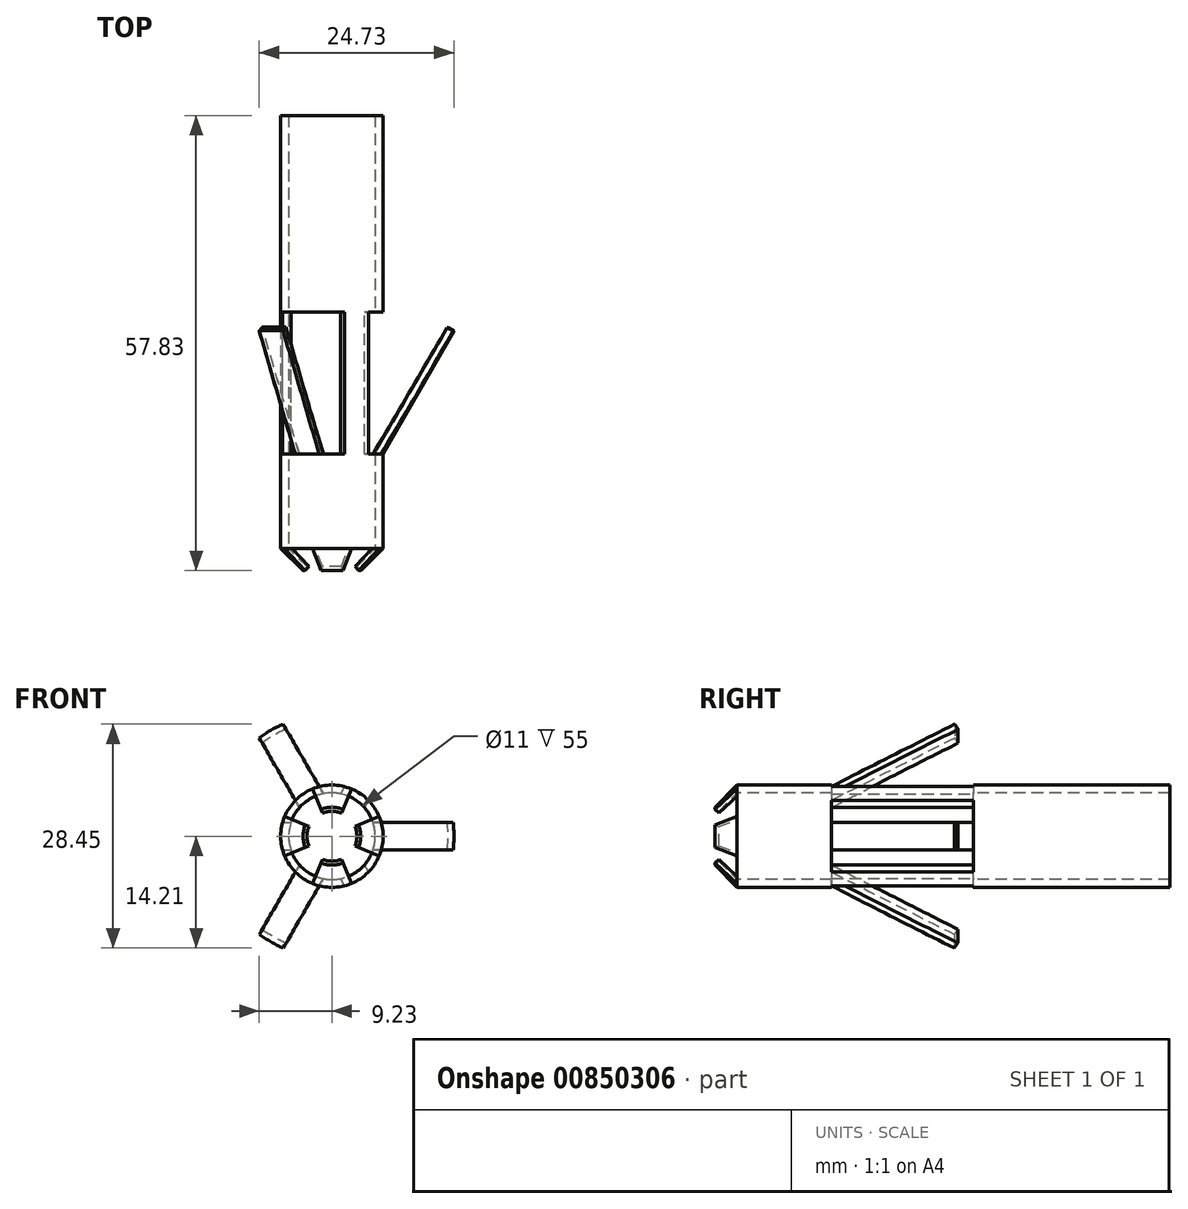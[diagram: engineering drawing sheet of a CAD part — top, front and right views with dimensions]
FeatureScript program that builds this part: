
annotation { "Feature Type Name" : "Feature", "Feature Type Description" : "" }
export const myFeature = defineFeature(function(context is Context, id is Id, definition is map)
    precondition{}
    {
        {
            var Q0;
            Q0=qCreatedBy(makeId("Front.planeOp"),FACE);
            var sketch = newSketch(context, id + "F0", { "sketchPlane" : qUnion([Q0])});
            skCircle(sketch, "E0", {"center": v(0, 0) * mm, "radius": 6.5 * mm});
            skSolve(sketch);
        }
        {
            var Q0;
            Q0 = qSketchRegion(id + "F0", true);
            extrude(context, id + "F1", {"entities" : qUnion([Q0]), "oppositeDirection" : true, "depth" : 30 * mm, "offsetDistance" : 25 * mm});
        }
        {
            var Q0;
            Q0=makeQuery(id+"F1.opExtrude","CAP_FACE",FACE,{"disambiguationData":[OSD([sQuery(id+"F0.wireOp",EDGE,"E0")])],"isStart":true});
            var Q1;
            Q1=makeQuery(id+"F1.opExtrude","CAP_FACE",FACE,{"disambiguationData":[OSD([sQuery(id+"F0.wireOp",EDGE,"E0")])],"isStart":false});
            shell(context, id + "F2", {"entities" : qUnion([Q0, Q1]), "thickness" : 1 * mm});
        }
        {
            var Q0;
            Q0=qCreatedBy(makeId("Top.planeOp"),FACE);
            var sketch = newSketch(context, id + "F3", { "sketchPlane" : qUnion([Q0])});
            skLineSegment(sketch, "E1", {"start": v(6.5, 0) * mm, "end": v(3.67, -2.83) * mm});
            skLineSegment(sketch, "E2", {"start": v(3.67, -2.83) * mm, "end": v(3.17, -2.33) * mm});
            skLineSegment(sketch, "E3", {"start": v(5.5, 0) * mm, "end": v(6.5, 0) * mm});
            skLineSegment(sketch, "E4", {"start": v(3.17, -2.33) * mm, "end": v(5.5, 0) * mm});
            skLineSegment(sketch, "E5", {"start": v(0, 1.69) * mm, "end": v(0, -1.88) * mm, "construction": true});
            skLineSegment(sketch, "E6.MirrorCS", {"start": v(-6.5, 0) * mm, "end": v(-3.67, -2.83) * mm});
            skLineSegment(sketch, "E7.MirrorCS", {"start": v(-3.67, -2.83) * mm, "end": v(-3.17, -2.33) * mm});
            skLineSegment(sketch, "E8.MirrorCS", {"start": v(-3.17, -2.33) * mm, "end": v(-5.5, 0) * mm});
            skLineSegment(sketch, "E9.MirrorCS", {"start": v(0, -1.69) * mm, "end": v(0, 1.88) * mm, "construction": true});
            skLineSegment(sketch, "E10.MirrorCS", {"start": v(-5.5, 0) * mm, "end": v(-6.5, 0) * mm});
            skPoint(sketch, "E11.MirrorCS.end.orphan", {"position": v(3.62, -5.5) * mm});
            skPoint(sketch, "E11.MirrorCS.start.orphan", {"position": v(7.19, -5.5) * mm});
            skSolve(sketch);
        }
        {
            var Q0;
            Q0=makeQuery(id+"F3.imprint","IMPRINT",FACE,{"disambiguationData":[TD([[makeQuery(id+"F3.imprint","IMPRINT",EDGE,{"derivedFrom":sQuery(id+"F3.wireOp",EDGE,"E1")}),-1.0]])]});
            var Q1;
            Q1=sQuery(id+"F3.wireOp",EDGE,"E9.MirrorCS");
            revolve(context, id + "F4", {"operationType" : NewBodyOperationType.ADD, "surfaceOperationType" : NewSurfaceOperationType.NEW, "entities" : qUnion([Q0]), "axis" : qUnion([Q1]), "revolveType" : RevolveType.SYMMETRIC, "angle" : 45 * degree});
        }
        {
            var Q0;
            Q0=qCreatedBy(makeId("Right.planeOp"),FACE);
            var sketch = newSketch(context, id + "F5", { "sketchPlane" : qUnion([Q0])});
            skLineSegment(sketch, "E12", {"start": v(0, 6.5) * mm, "end": v(-2.83, 3.67) * mm});
            skLineSegment(sketch, "E13", {"start": v(0, 5.5) * mm, "end": v(0, 6.5) * mm});
            skLineSegment(sketch, "E14", {"start": v(-2.83, 3.67) * mm, "end": v(-2.33, 3.17) * mm});
            skLineSegment(sketch, "E15", {"start": v(-2.33, 3.17) * mm, "end": v(0, 5.5) * mm});
            skLineSegment(sketch, "E16.MirrorCS", {"start": v(-2.83, -3.67) * mm, "end": v(-2.33, -3.17) * mm});
            skLineSegment(sketch, "E17.MirrorCS", {"start": v(-2.33, -3.17) * mm, "end": v(0, -5.5) * mm});
            skLineSegment(sketch, "E18.MirrorCS", {"start": v(0, -6.5) * mm, "end": v(-2.83, -3.67) * mm});
            skLineSegment(sketch, "E19.MirrorCS", {"start": v(0, -5.5) * mm, "end": v(0, -6.5) * mm});
            skSolve(sketch);
        }
        {
            var Q0;
            Q0 = qSketchRegion(id + "F5", true);
            var Q1;
            Q1=sQuery(id+"F3.wireOp",EDGE,"E9.MirrorCS");
            revolve(context, id + "F6", {"operationType" : NewBodyOperationType.ADD, "surfaceOperationType" : NewSurfaceOperationType.NEW, "entities" : qUnion([Q0]), "axis" : qUnion([Q1]), "revolveType" : RevolveType.SYMMETRIC, "angle" : 45 * degree});
        }
        {
            var Q0;
            Q0=makeQuery(id+"F1.opExtrude","CAP_FACE",FACE,{"disambiguationData":[OSD([sQuery(id+"F0.wireOp",EDGE,"E0")])],"isStart":false});
            var sketch = newSketch(context, id + "F7", { "sketchPlane" : qUnion([Q0])});
            skLineSegment(sketch, "E20", {"start": v(-7.69, 0) * mm, "end": v(7.71, 0) * mm, "construction": true});
            skArc(sketch, "E21", {"start": v(-6.26, 1.75) * mm, "mid": v(0, -6.5) * mm, "end": v(6.26, 1.75) * mm});
            skArc(sketch, "E22", {"start": v(-5.21, 1.75) * mm, "mid": v(0, -5.5) * mm, "end": v(5.21, 1.75) * mm});
            skArc(sketch, "E23", {"start": v(-6.5, 0) * mm, "mid": v(-6.44, 0.88) * mm, "end": v(-6.26, 1.75) * mm});
            skArc(sketch, "E24", {"start": v(-6.5, 0) * mm, "mid": v(-6.44, -0.88) * mm, "end": v(-6.26, -1.75) * mm});
            skArc(sketch, "E25", {"start": v(-5.5, 0) * mm, "mid": v(-5.43, 0.89) * mm, "end": v(-5.21, 1.75) * mm});
            skArc(sketch, "E26", {"start": v(-5.5, 0) * mm, "mid": v(-5.43, -0.89) * mm, "end": v(-5.21, -1.75) * mm});
            skLineSegment(sketch, "E27", {"start": v(-6.26, 1.75) * mm, "end": v(-5.21, 1.75) * mm});
            skLineSegment(sketch, "E28", {"start": v(-6.26, -1.75) * mm, "end": v(-5.21, -1.75) * mm});
            skLineSegment(sketch, "E29", {"start": v(0, -1.58) * mm, "end": v(0, 1.69) * mm, "construction": true});
            skLineSegment(sketch, "E30.MirrorCS", {"start": v(6.26, 1.75) * mm, "end": v(5.21, 1.75) * mm});
            skLineSegment(sketch, "E31.1.0", {"start": v(-1.61, 6.3) * mm, "end": v(-1.1, 5.4) * mm});
            skArc(sketch, "E31.1.1", {"start": v(-1.1, 5.4) * mm, "mid": v(-4.76, -2.75) * mm, "end": v(4.12, -3.64) * mm});
            skLineSegment(sketch, "E31.1.2", {"start": v(-4.65, 4.55) * mm, "end": v(-4.12, 3.64) * mm});
            skArc(sketch, "E31.1.3", {"start": v(-1.61, 6.3) * mm, "mid": v(-5.63, -3.25) * mm, "end": v(4.65, -4.55) * mm});
            skLineSegment(sketch, "E31.2.0", {"start": v(4.65, 4.55) * mm, "end": v(4.12, 3.64) * mm});
            skArc(sketch, "E31.2.1", {"start": v(4.12, 3.64) * mm, "mid": v(-4.76, 2.75) * mm, "end": v(-1.1, -5.4) * mm});
            skLineSegment(sketch, "E31.2.2", {"start": v(1.61, 6.3) * mm, "end": v(1.1, 5.4) * mm});
            skArc(sketch, "E31.2.3", {"start": v(4.65, 4.55) * mm, "mid": v(-5.63, 3.25) * mm, "end": v(-1.61, -6.3) * mm});
            skLineSegment(sketch, "E31.3.0", {"start": v(6.26, -1.75) * mm, "end": v(5.21, -1.75) * mm});
            skArc(sketch, "E31.3.1", {"start": v(5.21, -1.75) * mm, "mid": v(0, 5.5) * mm, "end": v(-5.21, -1.75) * mm});
            skArc(sketch, "E31.3.3", {"start": v(6.26, -1.75) * mm, "mid": v(0, 6.5) * mm, "end": v(-6.26, -1.75) * mm});
            skLineSegment(sketch, "E31.4.0", {"start": v(1.61, -6.3) * mm, "end": v(1.1, -5.4) * mm});
            skArc(sketch, "E31.4.1", {"start": v(1.1, -5.4) * mm, "mid": v(4.76, 2.75) * mm, "end": v(-4.12, 3.64) * mm});
            skLineSegment(sketch, "E31.4.2", {"start": v(4.65, -4.55) * mm, "end": v(4.12, -3.64) * mm});
            skArc(sketch, "E31.4.3", {"start": v(1.61, -6.3) * mm, "mid": v(5.63, 3.25) * mm, "end": v(-4.65, 4.55) * mm});
            skLineSegment(sketch, "E31.5.0", {"start": v(-4.65, -4.55) * mm, "end": v(-4.12, -3.64) * mm});
            skArc(sketch, "E31.5.1", {"start": v(-4.12, -3.64) * mm, "mid": v(4.76, -2.75) * mm, "end": v(1.1, 5.4) * mm});
            skLineSegment(sketch, "E31.5.2", {"start": v(-1.61, -6.3) * mm, "end": v(-1.1, -5.4) * mm});
            skArc(sketch, "E31.5.3", {"start": v(-4.65, -4.55) * mm, "mid": v(5.63, -3.25) * mm, "end": v(1.61, 6.3) * mm});
            skLineSegment(sketch, "E31.anchor1", {"start": v(0, 0) * mm, "end": v(-6.26, 1.75) * mm, "construction": true});
            skLineSegment(sketch, "E31.anchor2", {"start": v(0, 0) * mm, "end": v(-4.65, -4.55) * mm, "construction": true});
            skSolve(sketch);
        }
        {
            var Q0;
            {var subQ0=sQuery(id+"F7.wireOp",EDGE,"E27");Q0=makeQuery(id+"F7.imprint","IMPRINT",FACE,{"disambiguationData":[TD([[makeQuery(id+"F7.imprint","IMPRINT",EDGE,{"derivedFrom":subQ0}),1.0]])]});}
            var Q1;
            {var subQ0=sQuery(id+"F7.wireOp",EDGE,"E31.1.0");Q1=makeQuery(id+"F7.imprint","IMPRINT",FACE,{"disambiguationData":[TD([[makeQuery(id+"F7.imprint","IMPRINT",EDGE,{"derivedFrom":subQ0}),1.0]])]});}
            var Q2;
            {var subQ0=sQuery(id+"F7.wireOp",EDGE,"E31.2.0");Q2=makeQuery(id+"F7.imprint","IMPRINT",FACE,{"disambiguationData":[TD([[makeQuery(id+"F7.imprint","IMPRINT",EDGE,{"derivedFrom":subQ0}),1.0]])]});}
            var Q3;
            {var subQ0=sQuery(id+"F7.wireOp",EDGE,"E31.3.0");Q3=makeQuery(id+"F7.imprint","IMPRINT",FACE,{"disambiguationData":[TD([[makeQuery(id+"F7.imprint","IMPRINT",EDGE,{"derivedFrom":subQ0}),1.0]])]});}
            var Q4;
            {var subQ0=sQuery(id+"F7.wireOp",EDGE,"E31.4.0");Q4=makeQuery(id+"F7.imprint","IMPRINT",FACE,{"disambiguationData":[TD([[makeQuery(id+"F7.imprint","IMPRINT",EDGE,{"derivedFrom":subQ0}),1.0]])]});}
            var Q5;
            Q5=makeQuery(id+"F7.imprint","IMPRINT",FACE,{"disambiguationData":[TD([[makeQuery(id+"F7.imprint","IMPRINT",EDGE,{"derivedFrom":sQuery(id+"F7.wireOp",EDGE,"E28")}),-1.0]])]});
            extrude(context, id + "F8", {"entities" : qUnion([Q0, Q1, Q2, Q3, Q4, Q5]), "operationType" : NewBodyOperationType.REMOVE, "oppositeDirection" : true, "depth" : 18 * mm, "offsetDistance" : 25 * mm});
        }
        {
            var Q0;
            {var subQ0=sQuery(id+"F7.wireOp",EDGE,"E27");Q0=makeQuery(id+"F7.imprint","IMPRINT",FACE,{"disambiguationData":[TD([[makeQuery(id+"F7.imprint","IMPRINT",EDGE,{"derivedFrom":subQ0}),-1.0]])]});}
            var Q1;
            {var subQ0=sQuery(id+"F0.wireOp",EDGE,"E0");Q1=makeQuery(id+"F8.boolean.opBoolean","SPLIT",FACE,{"disambiguationData":[TD([makeQuery(id+"F8.opExtrude","SWEPT_FACE",FACE,{"disambiguationData":[OSD([sQuery(id+"F7.wireOp",EDGE,"E31.4.0")])]})])],"derivedFrom":makeQuery(id+"F1.opExtrude","CAP_FACE",FACE,{"disambiguationData":[OSD([subQ0])],"isStart":false})});}
            var Q2;
            {var subQ0=sQuery(id+"F0.wireOp",EDGE,"E0");Q2=makeQuery(id+"F8.boolean.opBoolean","SPLIT",FACE,{"disambiguationData":[TD([makeQuery(id+"F8.opExtrude","SWEPT_FACE",FACE,{"disambiguationData":[OSD([sQuery(id+"F7.wireOp",EDGE,"E31.2.0")])]})])],"derivedFrom":makeQuery(id+"F1.opExtrude","CAP_FACE",FACE,{"disambiguationData":[OSD([subQ0])],"isStart":false})});}
            extrude(context, id + "F9", {"entities" : qUnion([Q0, Q1, Q2]), "operationType" : NewBodyOperationType.REMOVE, "oppositeDirection" : true, "depth" : 18 * mm, "offsetDistance" : 25 * mm});
        }
        {
            var Q0;
            Q0=qCreatedBy(makeId("Top.planeOp"),FACE);
            var sketch = newSketch(context, id + "F10", { "sketchPlane" : qUnion([Q0])});
            skLineSegment(sketch, "E32", {"start": v(0, 0) * mm, "end": v(0, 14.35) * mm, "construction": true});
            skLineSegment(sketch, "E33", {"start": v(4.69, 12) * mm, "end": v(-4.46, 12) * mm, "construction": true});
            skLineSegment(sketch, "E34", {"start": v(0, 12) * mm, "end": v(6.5, 12) * mm, "construction": true});
            skLineSegment(sketch, "E35", {"start": v(6.5, 12) * mm, "end": v(15.5, 27.59) * mm});
            skLineSegment(sketch, "E36", {"start": v(15.5, 27.59) * mm, "end": v(14.75, 28.02) * mm});
            skLineSegment(sketch, "E37", {"start": v(14.75, 28.02) * mm, "end": v(5.5, 12) * mm});
            skLineSegment(sketch, "E38", {"start": v(5.5, 12) * mm, "end": v(6.5, 12) * mm});
            skLineSegment(sketch, "E39", {"start": v(5.5, 12) * mm, "end": v(5.5, 17.27) * mm, "construction": true});
            skLineSegment(sketch, "E40", {"start": v(-4.46, 12) * mm, "end": v(0, 12) * mm, "construction": true});
            skPoint(sketch, "E41.orphan", {"position": v(-6.5, 12) * mm});
            skSolve(sketch);
        }
        {
            var Q0;
            Q0 = qSketchRegion(id + "F10", true);
            var Q1;
            Q1=sQuery(id+"F10.wireOp",EDGE,"E32");
            revolve(context, id + "F11", {"operationType" : NewBodyOperationType.ADD, "surfaceOperationType" : NewSurfaceOperationType.NEW, "entities" : qUnion([Q0]), "axis" : qUnion([Q1]), "revolveType" : RevolveType.SYMMETRIC, "angle" : 40 * degree});
        }
        {
            var Q0;
            Q0=qCreatedBy(makeId("Right.planeOp"),FACE);
            cPlane(context, id + "F12", {"entities" : qUnion([Q0]), "cplaneType" : CPlaneType.OFFSET, "offset" : 5 * mm, "width" : 150 * mm, "height" : 150 * mm});
        }
        {
            var Q0;
            Q0=qCreatedBy(id+"F12.planeOp",FACE);
            var sketch = newSketch(context, id + "F13", { "sketchPlane" : qUnion([Q0])});
            skLineSegment(sketch, "E42", {"start": v(0, 0) * mm, "end": v(16.57, 0) * mm, "construction": true});
            skLineSegment(sketch, "E43", {"start": v(12, -1.75) * mm, "end": v(12, 1.75) * mm});
            skPoint(sketch, "E44", {"position": v(12, 0) * mm});
            skLineSegment(sketch, "E45", {"start": v(12, 1.75) * mm, "end": v(29.75, 1.75) * mm});
            skLineSegment(sketch, "E46", {"start": v(29.75, 1.75) * mm, "end": v(29.75, 5.84) * mm});
            skLineSegment(sketch, "E47", {"start": v(29.75, 5.84) * mm, "end": v(12, 5.84) * mm});
            skLineSegment(sketch, "E48", {"start": v(12, 5.84) * mm, "end": v(12, 1.75) * mm});
            skLineSegment(sketch, "E49", {"start": v(12, -1.75) * mm, "end": v(29.75, -1.75) * mm});
            skLineSegment(sketch, "E50", {"start": v(29.75, -1.75) * mm, "end": v(29.75, -5.4) * mm});
            skLineSegment(sketch, "E51", {"start": v(29.75, -5.4) * mm, "end": v(12, -5.4) * mm});
            skLineSegment(sketch, "E52", {"start": v(12, -5.4) * mm, "end": v(12, -1.75) * mm});
            skSolve(sketch);
        }
        {
            var Q0;
            Q0=makeQuery(id+"F13.imprint","IMPRINT",FACE,{"disambiguationData":[TD([[makeQuery(id+"F13.imprint","IMPRINT",EDGE,{"derivedFrom":sQuery(id+"F13.wireOp",EDGE,"E49")}),-1.0]])]});
            var Q1;
            Q1=makeQuery(id+"F13.imprint","IMPRINT",FACE,{"disambiguationData":[TD([[makeQuery(id+"F13.imprint","IMPRINT",EDGE,{"derivedFrom":sQuery(id+"F13.wireOp",EDGE,"E45")}),1.0]])]});
            var Q2;
            Q2=makeQuery(id+"F11.opRevolve","SWEPT_FACE",FACE,{"disambiguationData":[OSD([sQuery(id+"F10.wireOp",EDGE,"E35")])]});
            extrude(context, id + "F14", {"entities" : qUnion([Q0, Q1]), "operationType" : NewBodyOperationType.REMOVE, "endBound" : BoundingType.UP_TO_SURFACE, "depth" : 25 * mm, "endBoundEntityFace" : qUnion([Q2]), "offsetDistance" : 25 * mm});
        }
        {
            var Q0;
            Q0=sQuery(id+"F3.wireOp",EDGE,"E9.MirrorCS");
            cPlane(context, id + "F15", {"entities" : qUnion([Q0]), "cplaneType" : CPlaneType.LINE_ANGLE, "offset" : 25 * mm, "angle" : 60 * degree, "width" : 150 * mm, "height" : 150 * mm});
        }
        {
            var Q0;
            Q0=qCreatedBy(id+"F15.planeOp",FACE);
            var sketch = newSketch(context, id + "F16", { "sketchPlane" : qUnion([Q0])});
            skLineSegment(sketch, "E53", {"start": v(12, 7.88) * mm, "end": v(12, -8.63) * mm, "construction": true});
            skLineSegment(sketch, "E54", {"start": v(0, 0) * mm, "end": v(12, 0) * mm, "construction": true});
            skPoint(sketch, "E54.endSnap0", {"position": v(12, -0.37) * mm});
            skLineSegment(sketch, "E55", {"start": v(10.5, 6.5) * mm, "end": v(16.61, 6.5) * mm, "construction": true});
            skLineSegment(sketch, "E56", {"start": v(12, 6.5) * mm, "end": v(27.65, 15.54) * mm});
            skLineSegment(sketch, "E57", {"start": v(27.65, 15.54) * mm, "end": v(28.08, 14.79) * mm});
            skLineSegment(sketch, "E58", {"start": v(28.08, 14.79) * mm, "end": v(12, 5.5) * mm});
            skLineSegment(sketch, "E59", {"start": v(12, 5.5) * mm, "end": v(12, 6.5) * mm});
            skSolve(sketch);
        }
        {
            var Q0;
            Q0 = qSketchRegion(id + "F16", true);
            var Q1;
            Q1=sQuery(id+"F16.wireOp",EDGE,"E54");
            revolve(context, id + "F17", {"operationType" : NewBodyOperationType.ADD, "surfaceOperationType" : NewSurfaceOperationType.NEW, "entities" : qUnion([Q0]), "axis" : qUnion([Q1]), "revolveType" : RevolveType.SYMMETRIC, "angle" : 40 * degree});
        }
        {
            var Q0;
            Q0=sQuery(id+"F3.wireOp",EDGE,"E9.MirrorCS");
            cPlane(context, id + "F18", {"entities" : qUnion([Q0]), "cplaneType" : CPlaneType.LINE_ANGLE, "offset" : 25 * mm, "angle" : 60 * degree, "oppositeDirection" : true, "width" : 150 * mm, "height" : 150 * mm});
        }
        {
            var Q0;
            Q0=qCreatedBy(id+"F18.planeOp",FACE);
            var sketch = newSketch(context, id + "F19", { "sketchPlane" : qUnion([Q0])});
            skLineSegment(sketch, "E60", {"start": v(-12, -7.33) * mm, "end": v(-12, 9.85) * mm, "construction": true});
            skLineSegment(sketch, "E61", {"start": v(0, 0) * mm, "end": v(-12.8, 0) * mm, "construction": true});
            skLineSegment(sketch, "E62", {"start": v(-10.46, -6.5) * mm, "end": v(-16.28, -6.5) * mm, "construction": true});
            skLineSegment(sketch, "E63", {"start": v(-12, -6.5) * mm, "end": v(-27.59, -15.5) * mm});
            skLineSegment(sketch, "E64", {"start": v(-27.59, -15.5) * mm, "end": v(-28.02, -14.75) * mm});
            skLineSegment(sketch, "E65", {"start": v(-28.02, -14.75) * mm, "end": v(-12, -5.5) * mm});
            skLineSegment(sketch, "E66", {"start": v(-12, -5.5) * mm, "end": v(-12, -6.5) * mm});
            skSolve(sketch);
        }
        {
            var Q0;
            Q0 = qSketchRegion(id + "F19", true);
            var Q1;
            Q1=sQuery(id+"F19.wireOp",EDGE,"E61");
            revolve(context, id + "F20", {"operationType" : NewBodyOperationType.ADD, "surfaceOperationType" : NewSurfaceOperationType.NEW, "entities" : qUnion([Q0]), "axis" : qUnion([Q1]), "revolveType" : RevolveType.SYMMETRIC, "angle" : 40 * degree});
        }
        {
            var Q0;
            Q0=sQuery(id+"F3.wireOp",EDGE,"E9.MirrorCS");
            cPlane(context, id + "F21", {"entities" : qUnion([Q0]), "cplaneType" : CPlaneType.LINE_ANGLE, "offset" : 25 * mm, "angle" : 30 * degree, "width" : 150 * mm, "height" : 150 * mm});
        }
        {
            var Q0;
            Q0=qCreatedBy(id+"F21.planeOp",FACE);
            cPlane(context, id + "F22", {"entities" : qUnion([Q0]), "cplaneType" : CPlaneType.OFFSET, "offset" : 4.8 * mm, "oppositeDirection" : true, "width" : 150 * mm, "height" : 150 * mm});
        }
        {
            var Q0;
            Q0=qCreatedBy(id+"F22.planeOp",FACE);
            var sketch = newSketch(context, id + "F23", { "sketchPlane" : qUnion([Q0])});
            skLineSegment(sketch, "E67", {"start": v(0, 3.69) * mm, "end": v(0, 29.43) * mm, "construction": true});
            skLineSegment(sketch, "E68", {"start": v(-8.04, 12) * mm, "end": v(13.3, 12) * mm, "construction": true});
            skLineSegment(sketch, "E69", {"start": v(-1.75, 12) * mm, "end": v(1.75, 12) * mm});
            skLineSegment(sketch, "E70.bottom", {"start": v(-1.75, 12) * mm, "end": v(-5.8, 12) * mm});
            skLineSegment(sketch, "E70.top", {"start": v(-1.75, 28.66) * mm, "end": v(-5.8, 28.66) * mm});
            skLineSegment(sketch, "E70.left", {"start": v(-1.75, 12) * mm, "end": v(-1.75, 28.66) * mm});
            skLineSegment(sketch, "E70.right", {"start": v(-5.8, 12) * mm, "end": v(-5.8, 28.66) * mm});
            skLineSegment(sketch, "E71.bottom", {"start": v(1.75, 12) * mm, "end": v(5.9, 12) * mm});
            skLineSegment(sketch, "E71.top", {"start": v(1.75, 28.54) * mm, "end": v(5.9, 28.54) * mm});
            skLineSegment(sketch, "E71.left", {"start": v(1.75, 12) * mm, "end": v(1.75, 28.54) * mm});
            skLineSegment(sketch, "E71.right", {"start": v(5.9, 12) * mm, "end": v(5.9, 28.54) * mm});
            skSolve(sketch);
        }
        {
            var Q0;
            Q0 = qSketchRegion(id + "F23", true);
            var Q1;
            Q1=makeQuery(id+"F20.opRevolve","SWEPT_FACE",FACE,{"disambiguationData":[OSD([sQuery(id+"F19.wireOp",EDGE,"E63")])]});
            extrude(context, id + "F24", {"entities" : qUnion([Q0]), "operationType" : NewBodyOperationType.REMOVE, "endBound" : BoundingType.UP_TO_SURFACE, "oppositeDirection" : true, "depth" : 25 * mm, "endBoundEntityFace" : qUnion([Q1]), "offsetDistance" : 25 * mm});
        }
        {
            var Q0;
            Q0=sQuery(id+"F3.wireOp",EDGE,"E9.MirrorCS");
            cPlane(context, id + "F25", {"entities" : qUnion([Q0]), "cplaneType" : CPlaneType.LINE_ANGLE, "offset" : 25 * mm, "angle" : 30 * degree, "oppositeDirection" : true, "width" : 150 * mm, "height" : 150 * mm});
        }
        {
            var Q0;
            Q0=qCreatedBy(id+"F25.planeOp",FACE);
            cPlane(context, id + "F26", {"entities" : qUnion([Q0]), "cplaneType" : CPlaneType.OFFSET, "offset" : 4.8 * mm, "width" : 150 * mm, "height" : 150 * mm});
        }
        {
            var Q0;
            Q0=qCreatedBy(id+"F26.planeOp",FACE);
            var sketch = newSketch(context, id + "F27", { "sketchPlane" : qUnion([Q0])});
            skLineSegment(sketch, "E72", {"start": v(7.77, 12) * mm, "end": v(-10.48, 12) * mm, "construction": true});
            skLineSegment(sketch, "E73", {"start": v(0, 8.2) * mm, "end": v(0, 19.02) * mm, "construction": true});
            skLineSegment(sketch, "E74", {"start": v(1.75, 12) * mm, "end": v(-1.75, 12) * mm});
            skLineSegment(sketch, "E75.bottom", {"start": v(1.75, 12) * mm, "end": v(5.97, 12) * mm});
            skLineSegment(sketch, "E75.top", {"start": v(1.75, 28.58) * mm, "end": v(5.97, 28.58) * mm});
            skLineSegment(sketch, "E75.left", {"start": v(1.75, 12) * mm, "end": v(1.75, 28.58) * mm});
            skLineSegment(sketch, "E75.right", {"start": v(5.97, 12) * mm, "end": v(5.97, 28.58) * mm});
            skLineSegment(sketch, "E76.bottom", {"start": v(-1.75, 12) * mm, "end": v(-5.77, 12) * mm});
            skLineSegment(sketch, "E76.top", {"start": v(-1.75, 28.47) * mm, "end": v(-5.77, 28.47) * mm});
            skLineSegment(sketch, "E76.left", {"start": v(-1.75, 12) * mm, "end": v(-1.75, 28.47) * mm});
            skLineSegment(sketch, "E76.right", {"start": v(-5.77, 12) * mm, "end": v(-5.77, 28.47) * mm});
            skSolve(sketch);
        }
        {
            var Q0;
            Q0 = qSketchRegion(id + "F27", true);
            var Q1;
            Q1=makeQuery(id+"F17.opRevolve","SWEPT_FACE",FACE,{"disambiguationData":[OSD([sQuery(id+"F16.wireOp",EDGE,"E56")])]});
            extrude(context, id + "F28", {"entities" : qUnion([Q0]), "operationType" : NewBodyOperationType.REMOVE, "endBound" : BoundingType.UP_TO_SURFACE, "depth" : 25 * mm, "endBoundEntityFace" : qUnion([Q1]), "offsetDistance" : 25 * mm});
        }
        {
            var Q0;
            {var subQ0=sQuery(id+"F0.wireOp",EDGE,"E0");Q0=makeQuery(id+"F8.boolean.opBoolean","SPLIT",FACE,{"disambiguationData":[TD([makeQuery(id+"F8.opExtrude","SWEPT_FACE",FACE,{"disambiguationData":[OSD([sQuery(id+"F7.wireOp",EDGE,"E31.5.0")])]})])],"derivedFrom":makeQuery(id+"F1.opExtrude","CAP_FACE",FACE,{"disambiguationData":[OSD([subQ0])],"isStart":false})});}
            cPlane(context, id + "F29", {"entities" : qUnion([Q0]), "cplaneType" : CPlaneType.OFFSET, "offset" : 0 * mm, "width" : 150 * mm, "height" : 150 * mm});
        }
        {
            var Q0;
            Q0=qCreatedBy(id+"F29.planeOp",FACE);
            var sketch = newSketch(context, id + "F30", { "sketchPlane" : qUnion([Q0])});
            skCircle(sketch, "E77", {"center": v(0, 0) * mm, "radius": 6.5 * mm});
            skCircle(sketch, "E78", {"center": v(0, 0) * mm, "radius": 5.5 * mm});
            skSolve(sketch);
        }
        {
            var Q0;
            Q0 = qSketchRegion(id + "F30", true);
            extrude(context, id + "F31", {"entities" : qUnion([Q0]), "operationType" : NewBodyOperationType.ADD, "depth" : 25 * mm, "offsetDistance" : 25 * mm});
        }
        {
            var Q0;
            Q0=makeQuery(id+"F3.imprint","IMPRINT",FACE,{"disambiguationData":[TD([[makeQuery(id+"F3.imprint","IMPRINT",EDGE,{"derivedFrom":sQuery(id+"F3.wireOp",EDGE,"E6.MirrorCS")}),1.0]])]});
            var Q1;
            Q1=sQuery(id+"F3.wireOp",EDGE,"E9.MirrorCS");
            revolve(context, id + "F32", {"operationType" : NewBodyOperationType.ADD, "surfaceOperationType" : NewSurfaceOperationType.NEW, "entities" : qUnion([Q0]), "axis" : qUnion([Q1]), "revolveType" : RevolveType.SYMMETRIC, "angle" : 45 * degree});
        }
    });
